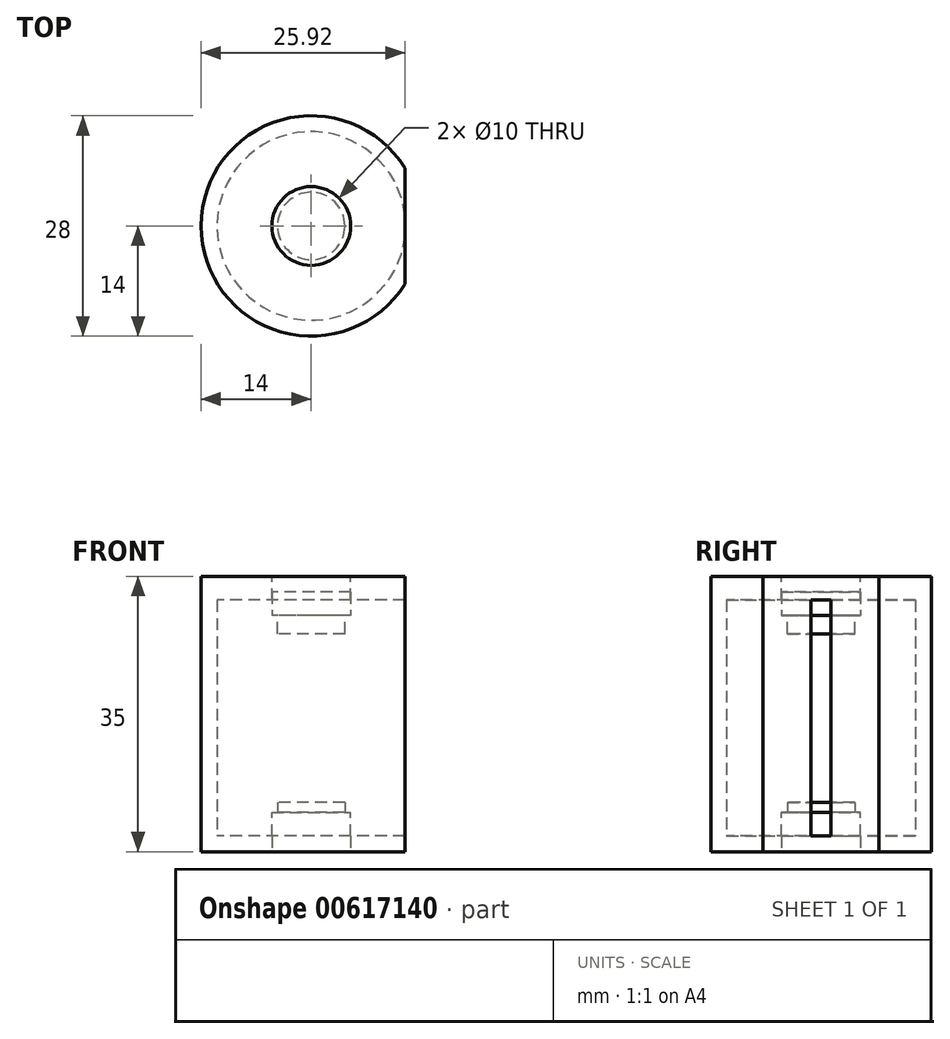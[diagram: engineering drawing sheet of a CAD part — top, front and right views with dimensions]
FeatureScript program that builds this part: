
annotation { "Feature Type Name" : "Feature", "Feature Type Description" : "" }
export const myFeature = defineFeature(function(context is Context, id is Id, definition is map)
    precondition{}
    {
        {
            var Q0;
            Q0=qCreatedBy(makeId("Top.planeOp"),FACE);
            var sketch = newSketch(context, id + "F0", { "sketchPlane" : qUnion([Q0])});
            skCircle(sketch, "E0", {"center": v(0, 0) * mm, "radius": 14 * mm});
            skSolve(sketch);
        }
        {
            var Q0;
            Q0=qCreatedBy(makeId("Top.planeOp"),FACE);
            var sketch = newSketch(context, id + "F1", { "sketchPlane" : qUnion([Q0])});
            skCircle(sketch, "E1", {"center": v(0, 0) * mm, "radius": 5 * mm});
            skSolve(sketch);
        }
        {
            var Q0;
            Q0 = qSketchRegion(id + "F0", true);
            extrude(context, id + "F2", {"entities" : qUnion([Q0]), "depth" : 35 * mm, "offsetDistance" : 25 * mm});
        }
        {
            var Q0;
            Q0=makeQuery(id+"F2.opExtrude","CAP_FACE",FACE,{"disambiguationData":[OSD([sQuery(id+"F0.wireOp",EDGE,"E0")])],"isStart":false});
            var sketch = newSketch(context, id + "F3", { "sketchPlane" : qUnion([Q0])});
            skCircle(sketch, "E2.0", {"center": v(0, 0) * mm, "radius": 5 * mm});
            skSolve(sketch);
        }
        {
            var Q0;
            Q0=makeQuery(id+"F3.imprint","IMPRINT",FACE,{"disambiguationData":[TD([[makeQuery(id+"F3.imprint","IMPRINT",EDGE,{"derivedFrom":sQuery(id+"F3.wireOp",EDGE,"E2.0")}),1.0]])]});
            extrude(context, id + "F4", {"entities" : qUnion([Q0]), "operationType" : NewBodyOperationType.REMOVE, "oppositeDirection" : true, "depth" : 5 * mm, "offsetDistance" : 25 * mm});
        }
        {
            var Q0;
            Q0=makeQuery(id+"F1.imprint","IMPRINT",FACE,{"disambiguationData":[TD([[makeQuery(id+"F1.imprint","IMPRINT",EDGE,{"derivedFrom":sQuery(id+"F1.wireOp",EDGE,"E1")}),1.0]])]});
            extrude(context, id + "F5", {"entities" : qUnion([Q0]), "operationType" : NewBodyOperationType.REMOVE, "oppositeDirection" : true, "depth" : -5 * mm, "offsetDistance" : 25 * mm});
        }
        {
            var Q0;
            Q0=makeQuery(id+"F2.opExtrude","SWEPT_BODY",BODY,{"disambiguationData":[OSD([sQuery(id+"F0.wireOp",EDGE,"E0")])]});
            transform(context, id + "F6", {"entities" : qUnion([Q0]), "transformType" : TransformType.TRANSLATION_3D, "dx" : 0 * mm, "dy" : 0 * mm, "dz" : -2 * mm, "makeCopy" : true});
        }
        {
            var Q0;
            Q0=makeQuery(id+"F2.opExtrude","SWEPT_BODY",BODY,{"disambiguationData":[OSD([sQuery(id+"F0.wireOp",EDGE,"E0")])]});
            var Q1;
            Q1=sQuery(id+"F0.wireOp",VERTEX,"E0.center");
            transform(context, id + "F7", {"entities" : qUnion([Q0]), "transformType" : TransformType.SCALE_UNIFORMLY, "scale" : 0.86, "scalePoint" : qUnion([Q1]), "makeCopy" : true});
        }
        {
            var Q0;
            Q0=makeQuery(id+"F2.opExtrude","SWEPT_BODY",BODY,{"disambiguationData":[OSD([sQuery(id+"F0.wireOp",EDGE,"E0")])]});
            deleteBodies(context, id + "F8", {"entities" : qUnion([Q0])});
        }
        {
            var Q0;
            Q0=makeQuery(id+"F7.opPattern","COPY",BODY,{"derivedFrom":makeQuery(id+"F2.opExtrude","SWEPT_BODY",BODY,{"disambiguationData":[OSD([sQuery(id+"F0.wireOp",EDGE,"E0")])]}),"instanceName":"1"});
            var Q1;
            Q1=makeQuery(id+"F6.opPattern","COPY",BODY,{"derivedFrom":makeQuery(id+"F2.opExtrude","SWEPT_BODY",BODY,{"disambiguationData":[OSD([sQuery(id+"F0.wireOp",EDGE,"E0")])]}),"instanceName":"1"});
            booleanBodies(context, id + "F9", {"operationType" : BooleanOperationType.SUBTRACTION, "tools" : qUnion([Q0]), "targets" : qUnion([Q1])});
        }
        {
            var Q0;
            Q0=makeQuery(id+"F6.opPattern","COPY",FACE,{"derivedFrom":makeQuery(id+"F4.boolean.opBoolean","COPY",FACE,{"derivedFrom":makeQuery(id+"F4.opExtrude","CAP_FACE",FACE,{"disambiguationData":[OSD([sQuery(id+"F3.wireOp",EDGE,"E2.0")])],"isStart":false})}),"instanceName":"1"});
            var sketch = newSketch(context, id + "F10", { "sketchPlane" : qUnion([Q0])});
            skCircle(sketch, "E3", {"center": v(0, 0) * mm, "radius": 5 * mm});
            skSolve(sketch);
        }
        {
            var Q0;
            Q0=makeQuery(id+"F10.imprint","IMPRINT",FACE,{"disambiguationData":[TD([[makeQuery(id+"F10.imprint","IMPRINT",EDGE,{"derivedFrom":sQuery(id+"F10.wireOp",EDGE,"E3")}),1.0]])]});
            var Q1;
            {var subQ0=sQuery(id+"F3.wireOp",EDGE,"E2.0");Q1=makeQuery(id+"F10.imprint","IMPRINT",FACE,{"disambiguationData":[TD([[makeQuery(id+"F10.imprint","IMPRINT",EDGE,{"derivedFrom":makeQuery(id+"F9.opBoolean","INTERSECT",EDGE,{"derivedFrom":[makeQuery(id+"F6.opPattern","COPY",FACE,{"derivedFrom":makeQuery(id+"F4.boolean.opBoolean","COPY",FACE,{"derivedFrom":makeQuery(id+"F4.opExtrude","CAP_FACE",FACE,{"disambiguationData":[OSD([subQ0])],"isStart":false})}),"instanceName":"1"}),makeQuery(id+"F7.opPattern","COPY",FACE,{"derivedFrom":makeQuery(id+"F4.boolean.opBoolean","COPY",FACE,{"derivedFrom":makeQuery(id+"F4.opExtrude","SWEPT_FACE",FACE,{"disambiguationData":[OSD([subQ0])]})}),"instanceName":"1"})]})}),1.0]])]});}
            extrude(context, id + "F11", {"entities" : qUnion([Q0, Q1]), "depth" : 3 * mm, "offsetDistance" : 25 * mm});
        }
        {
            var Q0;
            Q0=makeQuery(id+"F6.opPattern","COPY",FACE,{"derivedFrom":makeQuery(id+"F5.boolean.opBoolean","COPY",FACE,{"derivedFrom":makeQuery(id+"F5.opExtrude","CAP_FACE",FACE,{"disambiguationData":[OSD([sQuery(id+"F1.wireOp",EDGE,"E1")])],"isStart":false})}),"instanceName":"1"});
            var sketch = newSketch(context, id + "F12", { "sketchPlane" : qUnion([Q0])});
            skCircle(sketch, "E4", {"center": v(0, 0) * mm, "radius": 5 * mm});
            skSolve(sketch);
        }
        {
            var Q0;
            Q0=makeQuery(id+"F12.imprint","IMPRINT",FACE,{"disambiguationData":[TD([[makeQuery(id+"F12.imprint","IMPRINT",EDGE,{"derivedFrom":sQuery(id+"F12.wireOp",EDGE,"E4")}),1.0]])]});
            var Q1;
            {var subQ0=sQuery(id+"F1.wireOp",EDGE,"E1");Q1=makeQuery(id+"F12.imprint","IMPRINT",FACE,{"disambiguationData":[TD([[makeQuery(id+"F12.imprint","IMPRINT",EDGE,{"derivedFrom":makeQuery(id+"F9.opBoolean","INTERSECT",EDGE,{"derivedFrom":[makeQuery(id+"F6.opPattern","COPY",FACE,{"derivedFrom":makeQuery(id+"F5.boolean.opBoolean","COPY",FACE,{"derivedFrom":makeQuery(id+"F5.opExtrude","CAP_FACE",FACE,{"disambiguationData":[OSD([subQ0])],"isStart":false})}),"instanceName":"1"}),makeQuery(id+"F7.opPattern","COPY",FACE,{"derivedFrom":makeQuery(id+"F5.boolean.opBoolean","COPY",FACE,{"derivedFrom":makeQuery(id+"F5.opExtrude","SWEPT_FACE",FACE,{"disambiguationData":[OSD([subQ0])]})}),"instanceName":"1"})]})}),1.0]])]});}
            extrude(context, id + "F13", {"entities" : qUnion([Q0, Q1]), "operationType" : NewBodyOperationType.ADD, "depth" : 3 * mm, "offsetDistance" : 25 * mm});
        }
        {
            var Q0;
            Q0=makeQuery(id+"F6.opPattern","COPY",FACE,{"derivedFrom":makeQuery(id+"F2.opExtrude","CAP_FACE",FACE,{"disambiguationData":[OSD([sQuery(id+"F0.wireOp",EDGE,"E0")])],"isStart":false}),"instanceName":"1"});
            var sketch = newSketch(context, id + "F14", { "sketchPlane" : qUnion([Q0])});
            skLineSegment(sketch, "E5.bottom", {"start": v(11.92, -11.64) * mm, "end": v(22.92, -11.64) * mm});
            skLineSegment(sketch, "E5.top", {"start": v(11.92, 13.36) * mm, "end": v(22.92, 13.36) * mm});
            skLineSegment(sketch, "E5.left", {"start": v(11.92, -11.64) * mm, "end": v(11.92, 13.36) * mm});
            skLineSegment(sketch, "E5.right", {"start": v(22.92, -11.64) * mm, "end": v(22.92, 13.36) * mm});
            skSolve(sketch);
        }
        {
            var Q0;
            {var subQ4=sQuery(id+"F14.wireOp",EDGE,"E5.bottom");Q0=makeQuery(id+"F14.imprint","IMPRINT",FACE,{"disambiguationData":[TD([[makeQuery(id+"F14.imprint","IMPRINT",EDGE,{"derivedFrom":subQ4}),1.0]])]});}
            var Q1;
            {var subQ0=sQuery(id+"F14.wireOp",EDGE,"E5.left");var subQ1=makeQuery(id+"F6.opPattern","COPY",EDGE,{"derivedFrom":makeQuery(id+"F2.opExtrude","CAP_EDGE",EDGE,{"disambiguationData":[OSD([sQuery(id+"F0.wireOp",EDGE,"E0")])],"isStart":false}),"instanceName":"1"});var subQ2=makeQuery(id+"F14.imprint","INTERSECT",VERTEX,{"disambiguationData":[OD(0.0)],"derivedFrom":[subQ1,subQ0]});Q1=makeQuery(id+"F14.imprint","IMPRINT",FACE,{"disambiguationData":[TD([[makeQuery(id+"F14.imprint","IMPRINT",EDGE,{"disambiguationData":[TD([[subQ2,-1.0]])],"derivedFrom":subQ0}),-1.0]])]});}
            extrude(context, id + "F15", {"entities" : qUnion([Q0, Q1]), "operationType" : NewBodyOperationType.REMOVE, "oppositeDirection" : true, "depth" : 41.7 * mm, "offsetDistance" : 25 * mm});
        }
    });
